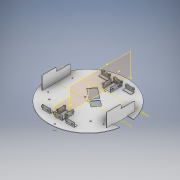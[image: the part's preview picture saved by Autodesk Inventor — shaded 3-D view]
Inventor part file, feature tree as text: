
AUTODESK INVENTOR PART (.ipt)
format: ipt  version: 2020 (Build 240168000, 168)  size: 646,144 bytes
history: native  units: mm
features: sketch x11, other x5, plane x3, extrude x1, pattern_circular x1
ambient origin geometry x8: Origin, YZ Plane, XZ Plane, XY Plane, X Axis, Y Axis, Z Axis, Center Point
bodies: Solid1 (feature_tree)
feature tree (21):
  other  "Gornja_konstrukcija_s_držačima_assembly.iam"
  other  "GornjaKonstrukcija_lidari_kamere_v.2.0.ipt:1"
  other  "5DržačaLidara.ipt:1"
  other  "5DržačaLidara.ipt:2"
  extrude  "Extrusion1"  Depth=2.0mm TaperAngle=0.0deg
  pattern_circular  "Circular Pattern1"  Count=2 Angle=180.0deg
  plane  "Work Plane1"
  plane  "Work Plane1_1"
  plane  "Work Plane3"
  other  "Work Axis1"
  sketch  "Sketch8"
  sketch  "Sketch8_1"  dims[d0=10.0mm d1=2.0mm d2=0.0mm d3=20.0mm d4=180.0deg]
  sketch  "Sketch8_2"
  sketch  "Sketch8_3"
  sketch  "Sketch8_4"
  sketch  "Sketch8_5"
  sketch  "Sketch8_1_1"
  sketch  "Sketch8_2_1"
  sketch  "Sketch8_3_1"
  sketch  "Sketch8_4_1"
  sketch  "Sketch12"
